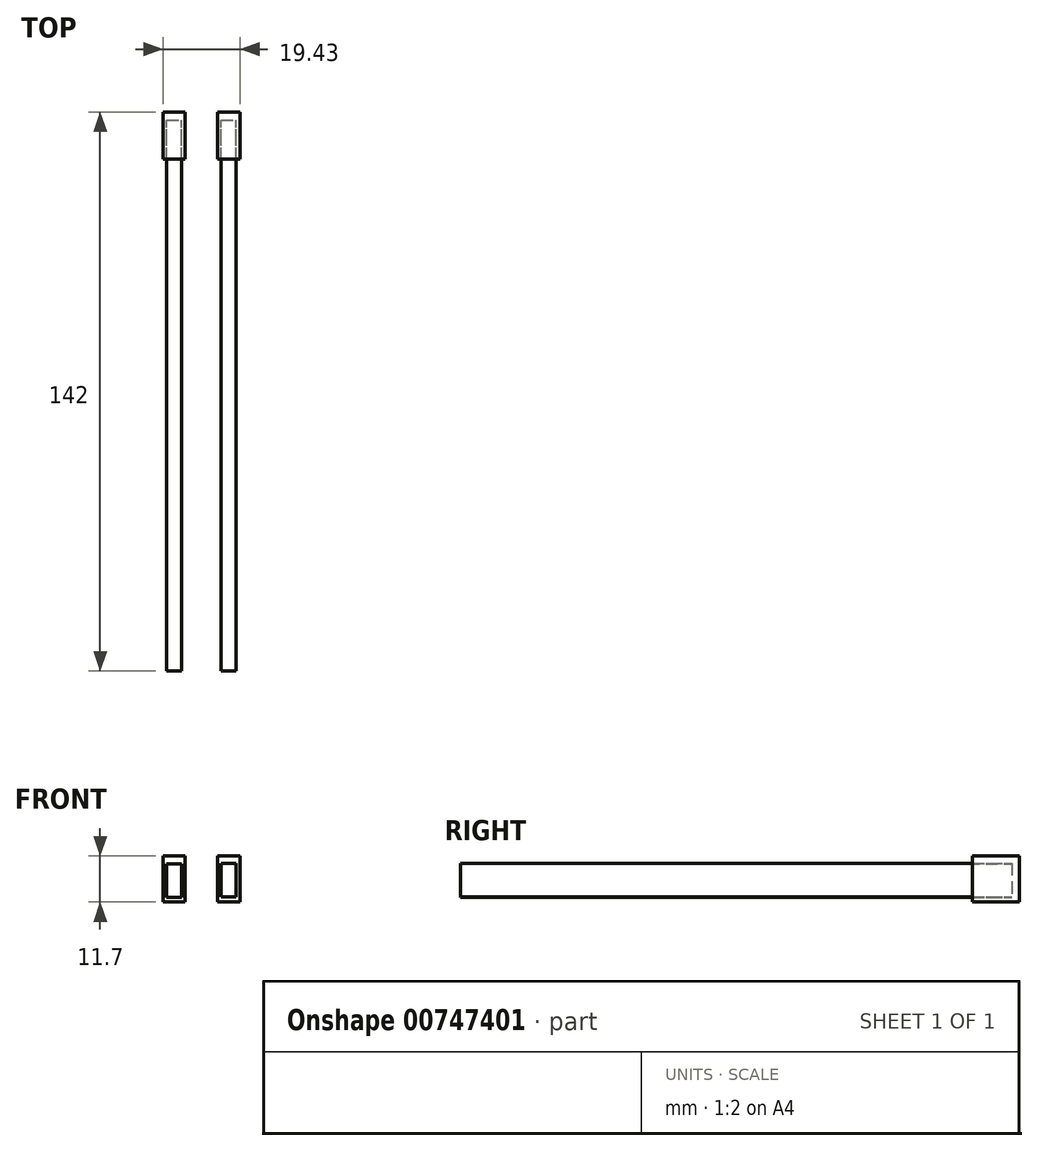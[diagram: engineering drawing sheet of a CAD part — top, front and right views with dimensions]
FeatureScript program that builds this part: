
annotation { "Feature Type Name" : "Feature", "Feature Type Description" : "" }
export const myFeature = defineFeature(function(context is Context, id is Id, definition is map)
    precondition{}
    {
        {
            var Q0;
            Q0=qCreatedBy(makeId("Front.planeOp"),FACE);
            var sketch = newSketch(context, id + "F0", { "sketchPlane" : qUnion([Q0])});
            skLineSegment(sketch, "E0.bottom", {"start": v(-37.11, 9.7) * mm, "end": v(-33.31, 9.7) * mm});
            skLineSegment(sketch, "E0.top", {"start": v(-37.11, 1.2) * mm, "end": v(-33.31, 1.2) * mm});
            skLineSegment(sketch, "E0.left", {"start": v(-37.11, 9.7) * mm, "end": v(-37.11, 1.2) * mm});
            skLineSegment(sketch, "E0.right", {"start": v(-33.31, 9.7) * mm, "end": v(-33.31, 1.2) * mm});
            skLineSegment(sketch, "E1.bottom", {"start": v(-23.31, 9.78) * mm, "end": v(-19.51, 9.78) * mm});
            skLineSegment(sketch, "E1.top", {"start": v(-23.31, 1.28) * mm, "end": v(-19.51, 1.28) * mm});
            skLineSegment(sketch, "E1.left", {"start": v(-23.31, 9.78) * mm, "end": v(-23.31, 1.28) * mm});
            skLineSegment(sketch, "E1.right", {"start": v(-19.51, 9.78) * mm, "end": v(-19.51, 1.28) * mm});
            skSolve(sketch);
        }
        {
            var Q0;
            Q0=makeQuery(id+"F0.imprint","IMPRINT",FACE,{"disambiguationData":[TD([[makeQuery(id+"F0.imprint","IMPRINT",EDGE,{"derivedFrom":sQuery(id+"F0.wireOp",EDGE,"E0.bottom")}),-1.0]])]});
            var Q1;
            Q1=makeQuery(id+"F0.imprint","IMPRINT",FACE,{"disambiguationData":[TD([[makeQuery(id+"F0.imprint","IMPRINT",EDGE,{"derivedFrom":sQuery(id+"F0.wireOp",EDGE,"E1.bottom")}),-1.0]])]});
            extrude(context, id + "F1", {"entities" : qUnion([Q0, Q1]), "depth" : 140 * mm, "offsetDistance" : 25 * mm});
        }
        {
            var Q0;
            Q0=qCreatedBy(makeId("Front.planeOp"),FACE);
            var sketch = newSketch(context, id + "F2", { "sketchPlane" : qUnion([Q0])});
            skLineSegment(sketch, "E2.bottom", {"start": v(-32.52, 0) * mm, "end": v(-37.98, 0) * mm});
            skLineSegment(sketch, "E2.top", {"start": v(-32.52, 11.7) * mm, "end": v(-37.98, 11.7) * mm});
            skLineSegment(sketch, "E2.left", {"start": v(-32.52, 0) * mm, "end": v(-32.52, 11.7) * mm});
            skLineSegment(sketch, "E2.right", {"start": v(-37.98, 0) * mm, "end": v(-37.98, 11.7) * mm});
            skPoint(sketch, "E2.middle", {"position": v(-35.25, 5.85) * mm});
            skLineSegment(sketch, "E3.bottom", {"start": v(-18.55, 0) * mm, "end": v(-24.26, 0) * mm});
            skLineSegment(sketch, "E3.top", {"start": v(-18.55, 11.7) * mm, "end": v(-24.26, 11.7) * mm});
            skLineSegment(sketch, "E3.left", {"start": v(-18.55, 0) * mm, "end": v(-18.55, 11.7) * mm});
            skLineSegment(sketch, "E3.right", {"start": v(-24.26, 0) * mm, "end": v(-24.26, 11.7) * mm});
            skPoint(sketch, "E3.middle", {"position": v(-21.4, 5.85) * mm});
            skSolve(sketch);
        }
        {
            var Q0;
            Q0=makeQuery(id+"F2.imprint","IMPRINT",FACE,{"disambiguationData":[TD([[makeQuery(id+"F2.imprint","IMPRINT",EDGE,{"derivedFrom":sQuery(id+"F2.wireOp",EDGE,"E2.bottom")}),-1.0]])]});
            var Q1;
            Q1=makeQuery(id+"F2.imprint","IMPRINT",FACE,{"disambiguationData":[TD([[makeQuery(id+"F2.imprint","IMPRINT",EDGE,{"derivedFrom":sQuery(id+"F2.wireOp",EDGE,"E3.bottom")}),-1.0]])]});
            extrude(context, id + "F3", {"entities" : qUnion([Q0, Q1]), "depth" : 10 * mm, "offsetDistance" : 25 * mm, "hasSecondDirection" : true, "secondDirectionOppositeDirection" : true, "secondDirectionDepth" : 2 * mm});
        }
    });
